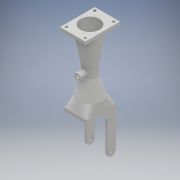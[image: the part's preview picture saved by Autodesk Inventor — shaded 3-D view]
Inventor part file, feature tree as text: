
AUTODESK INVENTOR PART (.ipt)
format: ipt  version: 2017 (Build 210142000, 142)  size: 399,872 bytes
history: native  units: mm
features: sketch x8, extrude x5, plane x4, projected_geometry x3, loft x2, other x2, revolve x1, fillet x1, chamfer x1, mirror x1
ambient origin geometry x8: Origin, YZ Plane, XZ Plane, XY Plane, X Axis, Y Axis, Z Axis, Center Point
bodies: Solid1 (feature_tree)
feature tree (28):
  extrude  "Extrusion1"  Depth=30.0mm
  plane  "Work Plane1"
  sketch  "Sketch2"  dims[d2=3.0mm d3=3.0mm]
  sketch  "Sketch3"  dims[d4=5.0mm d5=0.0mm d6=15.0mm]
  loft  "Loft1"
  loft  "Loft2"
  revolve  "Revolution1"  [1 undecoded]
  plane  "Work Plane3"
  extrude  "Extrusion2"  TaperAngle=0.0deg  [1 undecoded]
  fillet  "Fillet1"  [1 undecoded]
  extrude  "Extrusion3"  Depth=15.0mm
  chamfer  "Chamfer1"  Distance=5.0mm
  mirror  "Mirror1"
  extrude  "Extrusion4"  Depth=10.0mm
  plane  "Work Plane4"
  extrude  "Extrusion5"  Depth=10.0mm
  sketch  "Sketch1"  dims[d0=40.0mm d1=30.0mm]
  projected_geometry  "Projected Loop1"
  other  "Edges1"
  other  "Edges2"
  sketch  "Sketch5"  dims[d7=30.0mm d8=4.0mm]
  plane  "Work Plane2"
  sketch  "Sketch6"  dims[d9=0.0mm d10=90.0deg d11=0.0mm d12=90.0deg d13=0.0mm d14=90.0deg]
  sketch  "Sketch7"  dims[d15=0.0mm d16=90.0deg d19=15.0mm]
  projected_geometry  "Projected Loop3"
  sketch  "Sketch8"  dims[d20=4.0mm]
  sketch  "Sketch9"  dims[d22=3.490659mm d23=5.0mm d24=1.745329mm d25=8.0mm d26=15.0mm d27=5.0mm d28=4.0mm d29=5.0mm d30=5.0mm d31=4.0mm d32=90.0deg d33=5.0mm d34=55.0mm d35=40.0mm d36=4.0mm d37=45.0mm d38=30.0mm d39=5.0mm d40=0.0mm d41=30.0mm d42=62.0mm d43=36.2mm d44=4.5mm d45=6.0mm d46=0.0mm d47=10.0mm d48=2.0mm d49=45.0deg d50=5.0mm d51=6.0mm d52=0.0mm d53=-20.0mm d54=10.0mm d55=6.0mm d56=0.0mm]
  projected_geometry  "Projected Loop4"
note: 3 required parameter values undecoded (feature->parameter linkage not recoverable at this tier; creation-order binding heuristic only, values carry confidence <= 0.55)